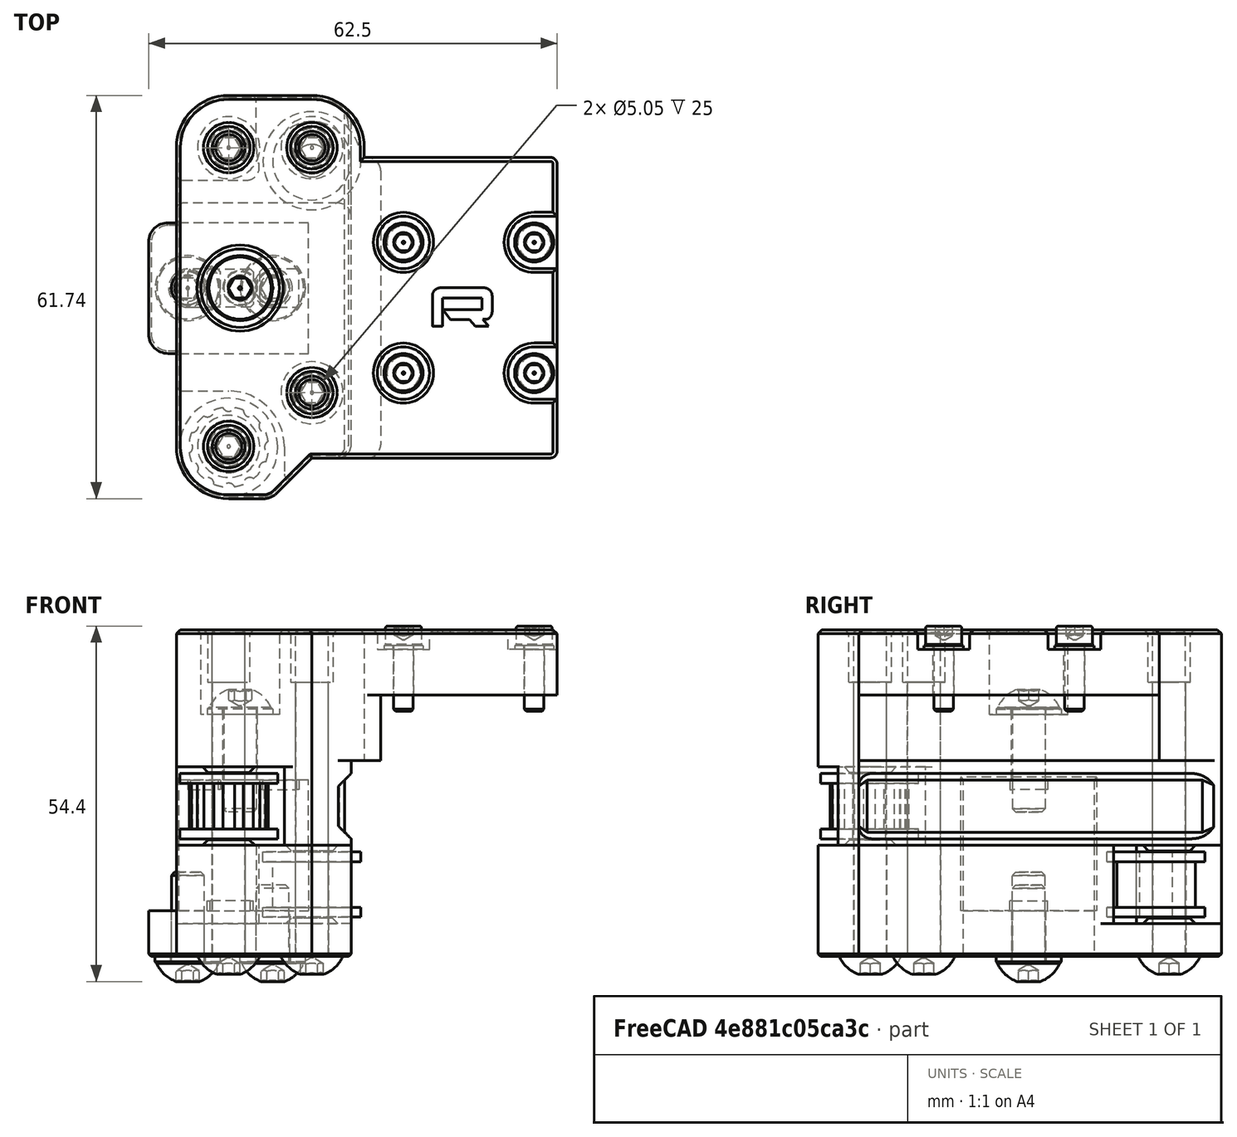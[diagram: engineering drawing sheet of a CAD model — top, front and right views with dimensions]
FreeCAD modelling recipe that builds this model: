
FCSTD DOCUMENT  (FreeCAD 0.19R24291 (Git))
Label: y-carrier-right-2020-assembly
License: Other
LicenseURL: GPL3
objects: Part::FeaturePython×18, Part::Feature×4, App::Part×1
note: 22 computed .brp shape members not serialized (recipe doc carries the construction recipe); baked Part::Feature solids carry a one-line shape summary decoded from their .brp

FEATURE [Part::Feature] Part__Mirroring002001  label="20t-idler"
  Placement = pos=(0,-4.61,0) rot=(0,0,1;0rad)
  shape: bbox 15 x 15 x 10 mm, 31 faces (baked)
FEATURE [Part::Feature] Part__Mirroring003001  label="smooth-idler"
  Placement = pos=(2,0.5,0) rot=(0,0,1;0rad)
  shape: bbox 15 x 15 x 10 mm, 8 faces (baked)
FEATURE [Part::Feature] Chamfer008001
  Placement = pos=(0,0,3) rot=(0,0,1;0rad)
  shape: bbox 31 x 61.74 x 17.85 mm, 86 faces (baked)
FEATURE [Part::FeaturePython] Washer  label="M5-Washer"  # Fasteners workbench fastener (typed FeaturePython)
  Placement = pos=(-28,0,3) rot=(-1,0,0;3.14159rad)
  baseObject = -> Chamfer008001 [Edge76]
  diameter = 1
  invert = false
  matchOuter = true
  offset = 0
  type = 4
FEATURE [Part::FeaturePython] Screw  label="M5x14-Screw"  # Fasteners workbench fastener (typed FeaturePython)
  Placement = pos=(-28,1e-16,1.9) rot=(-1,0,0;3.14159rad)
  baseObject = -> Washer [Edge1]
  diameter = 3
  invert = false
  length = 3
  lengthCustom = 14
  matchOuter = true
  offset = 0
  thread = false
  type = 39
FEATURE [Part::FeaturePython] Washer001  label="M5-Washer001"  # Fasteners workbench fastener (typed FeaturePython)
  Placement = pos=(-15,0,3) rot=(-1,0,0;3.14159rad)
  baseObject = -> Chamfer008001 [Edge80]
  diameter = 1
  invert = false
  matchOuter = true
  offset = 0
  type = 4
FEATURE [Part::FeaturePython] Screw001  label="M5x12-Screw"  # Fasteners workbench fastener (typed FeaturePython)
  Placement = pos=(-15,1e-16,1.9) rot=(-1,0,0;3.14159rad)
  baseObject = -> Washer001 [Edge1]
  diameter = 3
  invert = false
  length = 2
  lengthCustom = 12
  matchOuter = true
  offset = 0
  thread = false
  type = 39
FEATURE [Part::Feature] Cut002
  Placement = pos=(0,0,3) rot=(0,0,1;0rad)
  shape: bbox 58.24 x 61.74 x 33.85 mm, 150 faces (baked)
FEATURE [Part::FeaturePython] Screw002  label="M5x50-Screw"  # Fasteners workbench fastener (typed FeaturePython)
  Placement = pos=(-9,21.5,3) rot=(-1,0,0;3.14159rad)
  baseObject = -> Chamfer008001 [Edge84]
  diameter = 3
  invert = false
  length = 11
  lengthCustom = 50
  matchOuter = true
  offset = 0
  thread = false
  type = 39
FEATURE [Part::FeaturePython] Screw003  label="M5x50-Screw001"  # Fasteners workbench fastener (typed FeaturePython)
  Placement = pos=(-21.74,21.5,3) rot=(-1,0,0;3.14159rad)
  baseObject = -> Chamfer008001 [Edge82]
  diameter = 3
  invert = false
  length = 11
  lengthCustom = 50
  matchOuter = true
  offset = 0
  thread = false
  type = 39
FEATURE [Part::FeaturePython] Screw004  label="M5x50-Screw002"  # Fasteners workbench fastener (typed FeaturePython)
  Placement = pos=(-9,-16,3) rot=(-1,0,0;3.14159rad)
  baseObject = -> Chamfer008001 [Edge81]
  diameter = 3
  invert = false
  length = 11
  lengthCustom = 50
  matchOuter = true
  offset = 0
  thread = false
  type = 39
FEATURE [Part::FeaturePython] Screw005  label="M5x50-Screw003"  # Fasteners workbench fastener (typed FeaturePython)
  Placement = pos=(-21.74,-24.24,3) rot=(-1,0,0;3.14159rad)
  baseObject = -> Chamfer008001 [Edge83]
  diameter = 3
  invert = false
  length = 11
  lengthCustom = 50
  matchOuter = true
  offset = 0
  thread = false
  type = 39
FEATURE [Part::FeaturePython] Washer002  label="M3-Washer"  # Fasteners workbench fastener (typed FeaturePython)
  Placement = pos=(25,7,50) rot=(0,0,1;0rad)
  baseObject = -> Cut002 [Edge375]
  diameter = 4
  invert = true
  matchOuter = true
  offset = 0
  type = 5
FEATURE [Part::FeaturePython] Washer003  label="M3-Washer004"  # Fasteners workbench fastener (typed FeaturePython)
  Placement = pos=(25,-13,50) rot=(0,0,1;0rad)
  baseObject = -> Cut002 [Edge371]
  diameter = 4
  invert = true
  matchOuter = true
  offset = 0
  type = 5
FEATURE [Part::FeaturePython] Washer004  label="M3-Washer005"  # Fasteners workbench fastener (typed FeaturePython)
  Placement = pos=(5,-13,50) rot=(0,0,1;0rad)
  baseObject = -> Cut002 [Edge369]
  diameter = 4
  invert = true
  matchOuter = true
  offset = 0
  type = 5
FEATURE [Part::FeaturePython] Washer005  label="M3-Washer006"  # Fasteners workbench fastener (typed FeaturePython)
  Placement = pos=(5,7,50) rot=(0,0,1;0rad)
  baseObject = -> Cut002 [Edge373]
  diameter = 4
  invert = true
  matchOuter = true
  offset = 0
  type = 5
FEATURE [Part::FeaturePython] Screw006  label="M3x10-Screw"  # Fasteners workbench fastener (typed FeaturePython)
  Placement = pos=(25,-13,50.55) rot=(0,0,1;0rad)
  baseObject = -> Washer003 [Edge1]
  diameter = 4
  invert = false
  length = 3
  lengthCustom = 10
  matchOuter = true
  offset = 0
  thread = false
  type = 33
FEATURE [Part::FeaturePython] Screw007  label="M3x10-Screw001"  # Fasteners workbench fastener (typed FeaturePython)
  Placement = pos=(5,-13,50.55) rot=(0,0,1;0rad)
  baseObject = -> Washer004 [Edge1]
  diameter = 4
  invert = false
  length = 3
  lengthCustom = 10
  matchOuter = true
  offset = 0
  thread = false
  type = 33
FEATURE [Part::FeaturePython] Screw008  label="M3x10-Screw002"  # Fasteners workbench fastener (typed FeaturePython)
  Placement = pos=(5,7,50.55) rot=(0,0,1;0rad)
  baseObject = -> Washer005 [Edge1]
  diameter = 4
  invert = false
  length = 3
  lengthCustom = 10
  matchOuter = true
  offset = 0
  thread = false
  type = 33
FEATURE [Part::FeaturePython] Screw009  label="M3x10-Screw003"  # Fasteners workbench fastener (typed FeaturePython)
  Placement = pos=(25,7,50.55) rot=(0,0,1;0rad)
  baseObject = -> Washer002 [Edge1]
  diameter = 4
  invert = false
  length = 3
  lengthCustom = 10
  matchOuter = true
  offset = 0
  thread = false
  type = 33
FEATURE [Part::FeaturePython] Washer006  label="M5-Washer002"  # Fasteners workbench fastener (typed FeaturePython)
  Placement = pos=(-20,0,40) rot=(0,0,1;0rad)
  baseObject = -> Cut002 [Edge317]
  diameter = 1
  invert = false
  matchOuter = true
  offset = 0
  type = 4
FEATURE [Part::FeaturePython] Screw010  label="M5x16-Screw"  # Fasteners workbench fastener (typed FeaturePython)
  Placement = pos=(-20,0,41.1) rot=(0,0,1;0rad)
  baseObject = -> Washer006 [Edge1]
  diameter = 3
  invert = false
  length = 4
  lengthCustom = 16
  matchOuter = true
  offset = 0
  thread = false
  type = 39
FEATURE [App::Part] Part  label="Y-carrier-right"
  Group = -> [Part__Mirroring002001,Part__Mirroring003001,Chamfer008001,Cut002,Washer001,Screw,Screw001,Washer,Screw003,Screw004,Screw005,Screw002,Screw006,Screw009,Screw008,Screw007,Washer005,Washer004,Washer003,Washer002,Screw010,Washer006]
  Origin = -> Origin
